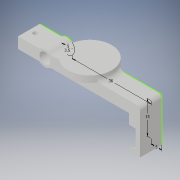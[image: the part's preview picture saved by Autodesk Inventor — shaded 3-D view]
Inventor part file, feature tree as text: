
AUTODESK INVENTOR PART (.ipt)
format: ipt  version: 2019 (Build 230136000, 136)  size: 165,888 bytes
history: native  units: in
note: dims shown in document units (in); Inventor stores cm internally (conversion verified against a paired STEP export)
features: fillet x7, sketch x4, extrude x3, hole x1
ambient origin geometry x8: Origin, YZ Plane, XZ Plane, XY Plane, X Axis, Y Axis, Z Axis, Center Point
bodies: Solid1 (feature_tree)
feature tree (15):
  sketch  "Sketch1"  dims[d6=0.1969in d7=0.1378in]
  extrude  "Extrusion1"  Depth=0.1378in
  extrude  "Extrusion2"  Depth=0.5906in
  fillet  "Fillet1"  Radius=0.1969in
  fillet  "Fillet2"  Radius=0.3937in
  fillet  "Fillet3"  Radius=0.7874in
  extrude  "Extrusion3"  Depth=0.0787in
  fillet  "Fillet4"  Radius=0.0787in
  fillet  "Fillet5"  Radius=0.0787in
  fillet  "Fillet6"  Radius=0.1181in
  fillet  "Fillet7"  Radius=0.0787in
  hole  "Hole2"  [1 undecoded]
  sketch  "Sketch2"  dims[d8=1.4173in d9=0.5906in d10=0.1969in d14=0.3937in d15=0.0in d16=0.7874in]
  sketch  "Sketch3"  dims[d17=0.1181in d18=0.0in d19=0.0787in d20=0.0787in d21=0.0787in d22=0.1181in d23=0.0in d24=0.0787in]
  sketch  "Sketch5"  dims[d25=0.0787in d26=0.0787in d27=0.0787in d35=0.0787in d36=0.2362in d37=0.1575in d38=0.0787in d39=90.0deg d40=0.0787in d41=0.0in d42=0.5191in]
note: 1 required parameter value undecoded (feature->parameter linkage not recoverable at this tier; creation-order binding heuristic only, values carry confidence <= 0.55)
